# Revit family: Sanitary_Installation-Systems_hansgrohe_01800XXX-hansgrohe-Basic-set-iBox-univer___
name_source: partatom
category: Plumbing Fixtures
revit_build: Autodesk Revit 2018 (Build: 20170223_1515(x64)
units: mm (PartAtom-declared; Revit-internal decimal feet)

## family parameters
Always vertical = No
Cut with Voids When Loaded = No
OmniClass Number = 23.27.31.29.11
OmniClass Title = Manual Mixing Valves
Part Type = Normal
Room Calculation Point = No
Round Connector Dimension = Use Diameter
Shared = No
Work Plane-Based = Yes

## types (1)
- 01800XXX hansgrohe Basic set iBox universal
    Always visible = Yes
    BIMobject category = Installation Systems
    Default Elevation = 1219.2 mm  [stored 4 ft]
    Description = 01800XXX hansgrohe Basic set iBox universal
    Diameter = 19 mm
    Edition number = 1
    IFC Classification = Sanitary Terminal
    Important Note = Please set up the System Classification and Flow Direction of each MEP connector in this product according to its intended use. For more information, check the installation manual in the manufacturer's website.
    Manufacturer = Hansgrohe
    Manufacturer name = hansgrohe
    Material 1 = Hansgrohe - Plastic - Green
    Material 2 = Hansgrohe - Plastic - Black
    Model = 01800XXX
    OmniClass Code = 23-27 31 29 11
    OmniClass Description = Manual Mixing Valves
    Product Guid = ec6dd5cb-2b38-49c2-a26a-172d7954ac03
    Product SKU = 01800XXX
    Product data url = https://bimobject.com
    Product family = hansgrohe
    Product group = Concealed Basic set bath/shower mixers
    Product name = 01800XXX hansgrohe Basic set iBox universal
    Product url = https://www.hansgrohe.com
    QR code = https://bimobject.com
    URL = https://www.hansgrohe.com
01800XXX hansgrohe Basic set iBox universal
    Weight Net (Kg) = 1

note: [stored X ft] marks values corroborated as IEEE doubles in the binary element streams (Revit-internal decimal feet)

## geometry (parser evidence)
native form markers: Sweep x3
no freeform markers — native parametric forms only
